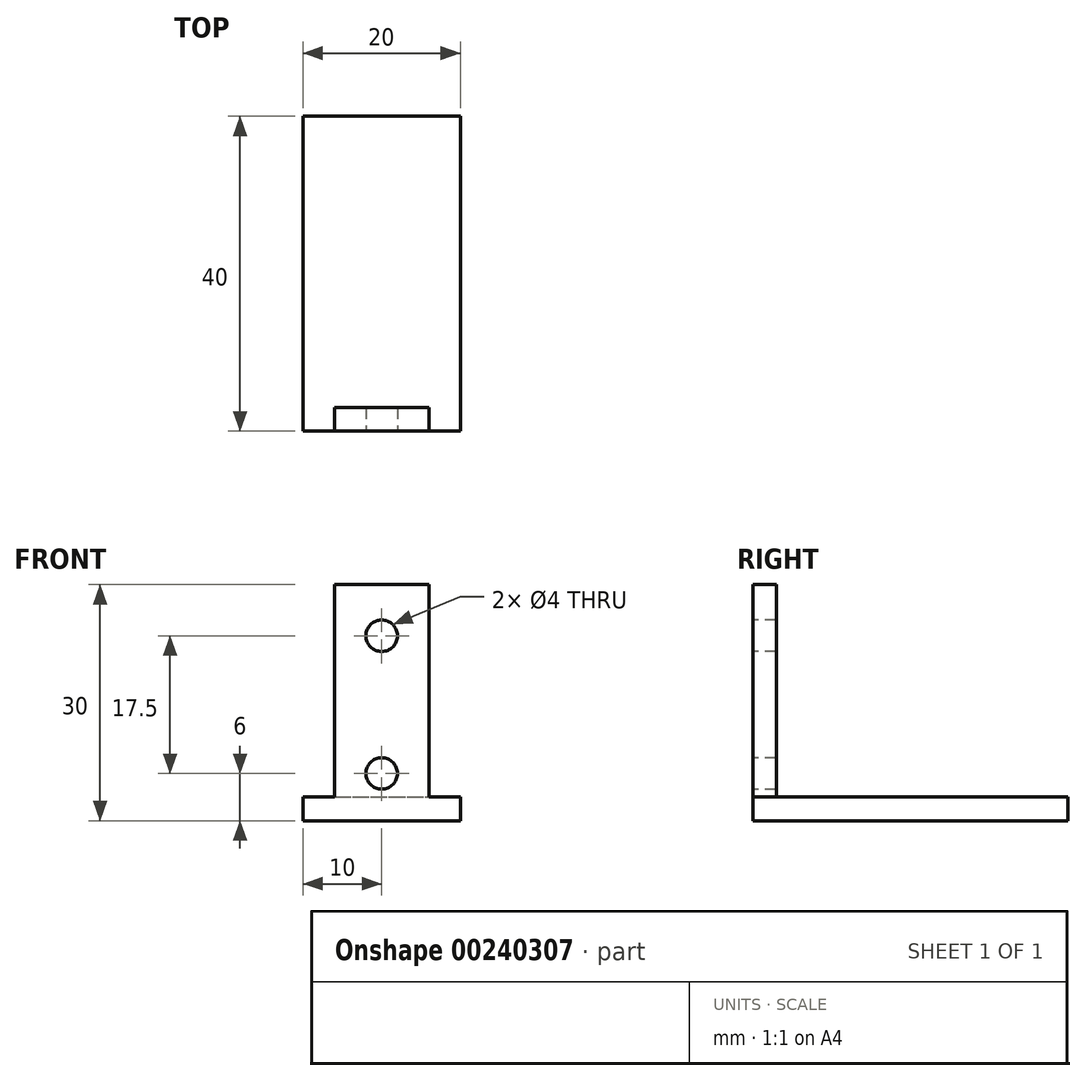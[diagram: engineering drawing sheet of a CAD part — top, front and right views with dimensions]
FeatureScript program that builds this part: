
annotation { "Feature Type Name" : "Feature", "Feature Type Description" : "" }
export const myFeature = defineFeature(function(context is Context, id is Id, definition is map)
    precondition{}
    {
        {
            var Q0;
            Q0=qCreatedBy(makeId("Top.planeOp"),FACE);
            var sketch = newSketch(context, id + "F0", { "sketchPlane" : qUnion([Q0])});
            skLineSegment(sketch, "E0.bottom", {"start": v(-10, 0) * mm, "end": v(10, 0) * mm});
            skLineSegment(sketch, "E0.top", {"start": v(-10, -40) * mm, "end": v(10, -40) * mm});
            skLineSegment(sketch, "E0.left", {"start": v(-10, 0) * mm, "end": v(-10, -40) * mm});
            skLineSegment(sketch, "E0.right", {"start": v(10, 0) * mm, "end": v(10, -40) * mm});
            skSolve(sketch);
        }
        {
            var Q0;
            Q0=qSketchRegion(id+"F0",true);
            extrude(context, id + "F1", {"entities" : qUnion([Q0]), "depth" : 3 * mm});
        }
        {
            var Q0;
            Q0=makeQuery(id+"F1.opExtrude","SWEPT_FACE",FACE,{"disambiguationData":[OSD([sQuery(id+"F0.wireOp",EDGE,"E0.top")])]});
            var sketch = newSketch(context, id + "F2", { "sketchPlane" : qUnion([Q0])});
            skLineSegment(sketch, "E1.bottom", {"start": v(-6, 0) * mm, "end": v(6, 0) * mm});
            skLineSegment(sketch, "E1.top", {"start": v(-6, 30) * mm, "end": v(6, 30) * mm});
            skLineSegment(sketch, "E1.left", {"start": v(-6, 0) * mm, "end": v(-6, 30) * mm});
            skLineSegment(sketch, "E1.right", {"start": v(6, 0) * mm, "end": v(6, 30) * mm});
            skCircle(sketch, "E2", {"center": v(0, 23.5) * mm, "radius": 2 * mm});
            skCircle(sketch, "E3", {"center": v(0, 6) * mm, "radius": 2 * mm});
            skSolve(sketch);
        }
        {
            var Q0;
            Q0=qSketchRegion(id+"F2",true);
            extrude(context, id + "F3", {"entities" : qUnion([Q0]), "operationType" : NewBodyOperationType.ADD, "oppositeDirection" : true, "depth" : 3 * mm});
        }
    });
